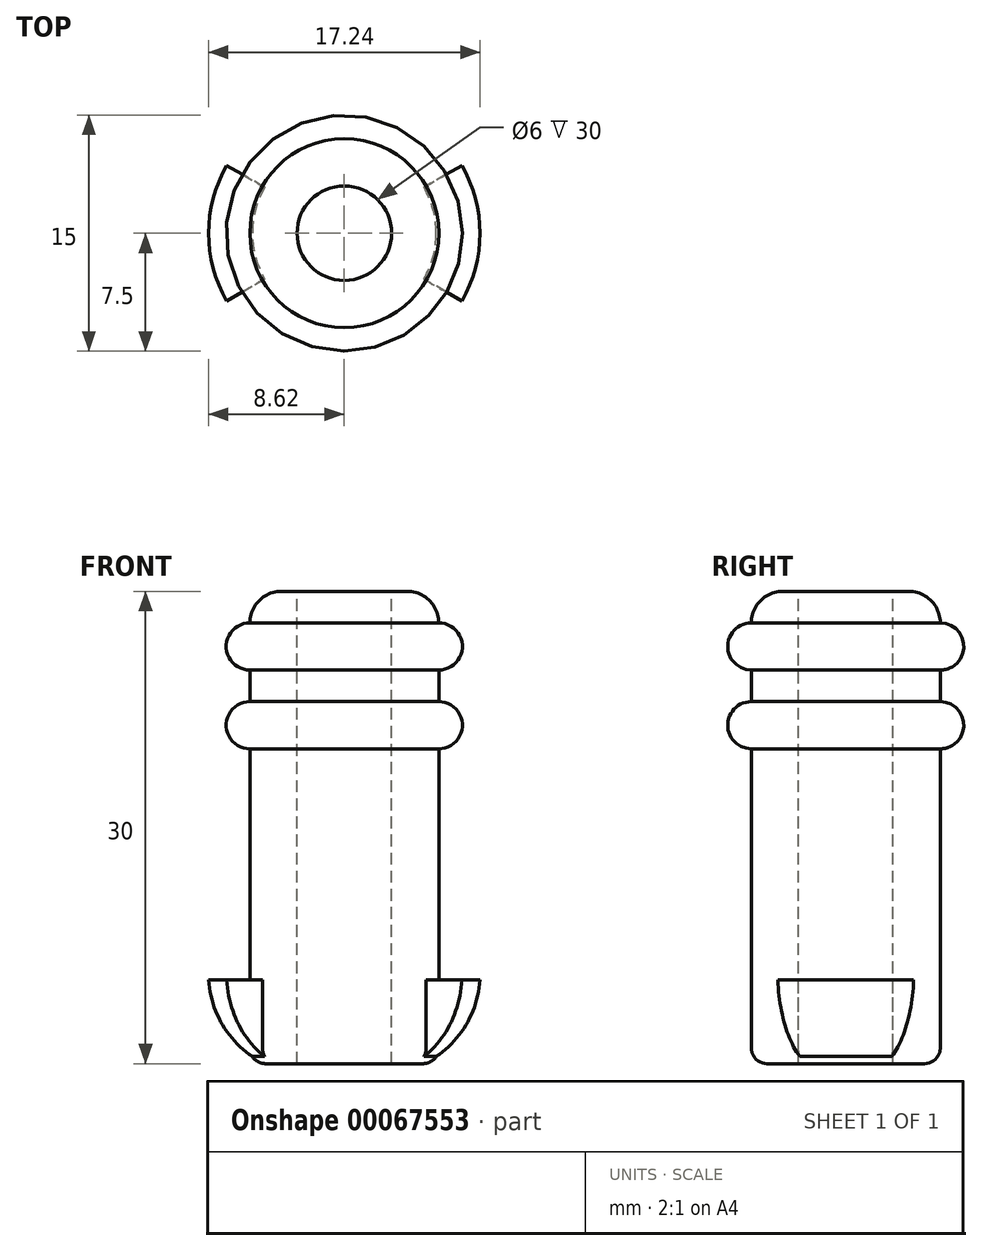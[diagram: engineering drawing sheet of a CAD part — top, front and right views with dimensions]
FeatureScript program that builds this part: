
annotation { "Feature Type Name" : "Feature", "Feature Type Description" : "" }
export const myFeature = defineFeature(function(context is Context, id is Id, definition is map)
    precondition{}
    {
        {
            var Q0;
            Q0=qCreatedBy(makeId("Front.planeOp"),FACE);
            var sketch = newSketch(context, id + "F0", { "sketchPlane" : qUnion([Q0])});
            skLineSegment(sketch, "E0", {"start": v(0, 0) * mm, "end": v(6, 0) * mm});
            skLineSegment(sketch, "E1", {"start": v(6, 0) * mm, "end": v(6, 15) * mm});
            skLineSegment(sketch, "E2", {"start": v(6, 30) * mm, "end": v(0, 30) * mm});
            skLineSegment(sketch, "E3", {"start": v(0, 30) * mm, "end": v(0, 0) * mm});
            skArc(sketch, "E4.0.1.0", {"start": v(6, 20) * mm, "mid": v(7.5, 21.5) * mm, "end": v(6, 23) * mm});
            skArc(sketch, "E4.0.2.0", {"start": v(6, 25) * mm, "mid": v(7.5, 26.5) * mm, "end": v(6, 28) * mm});
            skLineSegment(sketch, "E4.direction1", {"start": v(6, 15) * mm, "end": v(37, 15) * mm, "construction": true});
            skLineSegment(sketch, "E4.direction2", {"start": v(6, 15) * mm, "end": v(6, 20) * mm, "construction": true});
            skLineSegment(sketch, "E5.trimOffspring", {"start": v(6, 28) * mm, "end": v(6, 30) * mm});
            skLineSegment(sketch, "E6.trimOffspring", {"start": v(6, 23) * mm, "end": v(6, 25) * mm});
            skLineSegment(sketch, "E7.trimOffspring", {"start": v(6, 15) * mm, "end": v(6, 20) * mm});
            skSolve(sketch);
        }
        {
            var Q0;
            Q0=makeQuery(id+"F0.imprint","IMPRINT",FACE,{"disambiguationData":[TD([[makeQuery(id+"F0.imprint","IMPRINT",EDGE,{"derivedFrom":sQuery(id+"F0.wireOp",EDGE,"E0")}),1.0]])]});
            var Q1;
            Q1=sQuery(id+"F0.wireOp",EDGE,"E3");
            revolve(context, id + "F1", {"entities" : qUnion([Q0]), "axis" : qUnion([Q1]), "revolveType" : RevolveType.FULL});
        }
        {
            var Q0;
            Q0=makeQuery(id+"F1.opRevolve","SWEPT_FACE",FACE,{"disambiguationData":[OSD([sQuery(id+"F0.wireOp",EDGE,"E0")])]});
            var Q1;
            Q1=makeQuery(id+"F1.opRevolve","SWEPT_FACE",FACE,{"disambiguationData":[OSD([sQuery(id+"F0.wireOp",EDGE,"E2")])]});
            shell(context, id + "F2", {"entities" : qUnion([Q0, Q1]), "thickness" : 3 * mm});
        }
        {
            var Q0;
            Q0=makeQuery(id+"F1.opRevolve","SWEPT_EDGE",EDGE,{"disambiguationData":[OSD([sQuery(id+"F0.wireOp",EDGE,"E2"),sQuery(id+"F0.wireOp",EDGE,"E5.trimOffspring")])]});
            fillet(context, id + "F3", {"entities" : qUnion([Q0]), "radius" : 2 * mm, "tangentPropagation" : true, "allowEdgeOverflow" : false});
        }
        {
            var Q0;
            Q0=qCreatedBy(makeId("Front.planeOp"),FACE);
            var sketch = newSketch(context, id + "F4", { "sketchPlane" : qUnion([Q0])});
            skLineSegment(sketch, "E8", {"start": v(5.62, 0.3) * mm, "end": v(5.62, 5.3) * mm});
            skArc(sketch, "E9", {"start": v(5.62, 0.3) * mm, "mid": v(7.72, 2.45) * mm, "end": v(8.62, 5.3) * mm});
            skLineSegment(sketch, "E10", {"start": v(8.62, 5.3) * mm, "end": v(5.62, 5.3) * mm});
            skSolve(sketch);
        }
        {
            var Q0;
            Q0=makeQuery(id+"F4.imprint","IMPRINT",FACE,{"disambiguationData":[TD([[makeQuery(id+"F4.imprint","IMPRINT",EDGE,{"derivedFrom":sQuery(id+"F4.wireOp",EDGE,"E8")}),-1.0]])]});
            var Q1;
            Q1=makeQuery(id+"F1.opRevolve","SWEPT_EDGE",EDGE,{"disambiguationData":[OSD([sQuery(id+"F0.wireOp",EDGE,"E0"),sQuery(id+"F0.wireOp",EDGE,"E1")])]});
            revolve(context, id + "F5", {"operationType" : NewBodyOperationType.ADD, "entities" : qUnion([Q0]), "axis" : qUnion([Q1]), "revolveType" : RevolveType.TWO_DIRECTIONS, "angle" : 30 * degree, "angleBack" : 330 * degree});
        }
        {
            var Q0;
            Q0=makeQuery(id+"F1.opRevolve","SWEPT_BODY",BODY,{"disambiguationData":[OSD([sQuery(id+"F0.wireOp",EDGE,"E0"),sQuery(id+"F0.wireOp",EDGE,"E1"),sQuery(id+"F0.wireOp",EDGE,"E2"),sQuery(id+"F0.wireOp",EDGE,"E3"),sQuery(id+"F0.wireOp",EDGE,"91c724ac-c31c-48cf-b2e1-a4ecd234711a"),sQuery(id+"F0.wireOp",EDGE,"E4.0.1.0"),sQuery(id+"F0.wireOp",EDGE,"E4.0.2.0"),sQuery(id+"F0.wireOp",EDGE,"E5.trimOffspring"),sQuery(id+"F0.wireOp",EDGE,"E6.trimOffspring"),sQuery(id+"F0.wireOp",EDGE,"E7.trimOffspring")])]});
            var Q1;
            Q1=qCreatedBy(makeId("Right.planeOp"),FACE);
            mirror(context, id + "F6", {"operationType" : NewBodyOperationType.ADD, "entities" : qUnion([Q0]), "mirrorPlane" : qUnion([Q1])});
        }
        {
            var Q0;
            Q0=makeQuery(id+"F1.opRevolve","SWEPT_EDGE",EDGE,{"disambiguationData":[OSD([sQuery(id+"F0.wireOp",EDGE,"E0"),sQuery(id+"F0.wireOp",EDGE,"E1")])]});
            fillet(context, id + "F7", {"entities" : qUnion([Q0]), "radius" : 1 * mm, "tangentPropagation" : true, "allowEdgeOverflow" : false});
        }
    });
